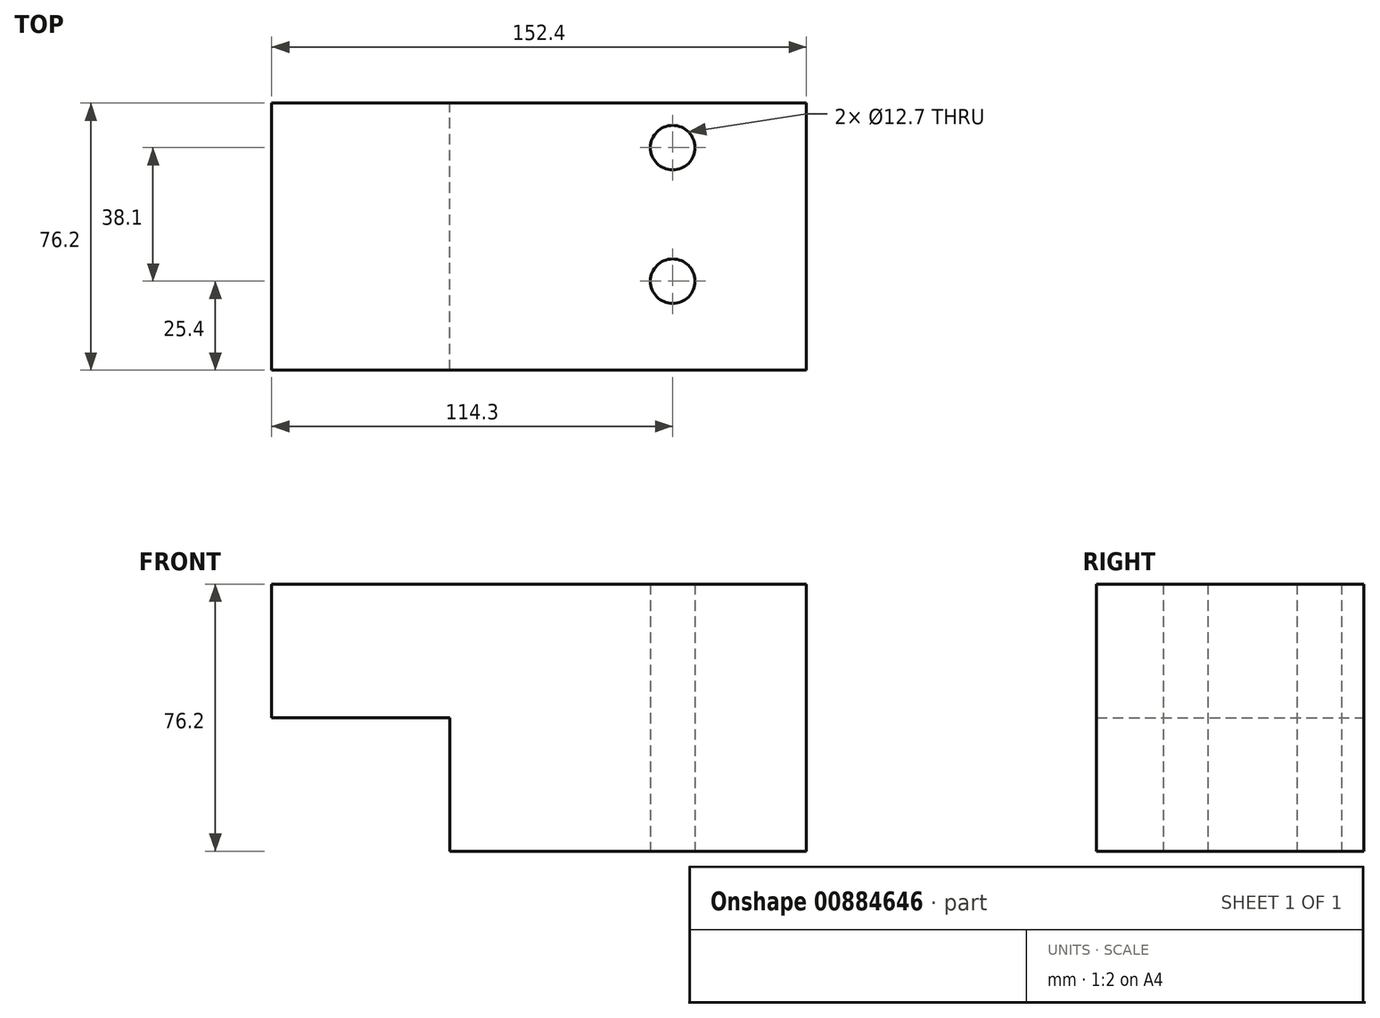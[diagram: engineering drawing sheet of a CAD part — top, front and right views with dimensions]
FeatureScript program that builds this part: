
annotation { "Feature Type Name" : "Feature", "Feature Type Description" : "" }
export const myFeature = defineFeature(function(context is Context, id is Id, definition is map)
    precondition{}
    {
        {
            var Q0;
            Q0=qCreatedBy(makeId("Top.planeOp"),FACE);
            var sketch = newSketch(context, id + "F0", { "sketchPlane" : qUnion([Q0])});
            skLineSegment(sketch, "E0.bottom", {"start": v(76.2, -38.1) * mm, "end": v(-76.2, -38.1) * mm});
            skLineSegment(sketch, "E0.top", {"start": v(76.2, 38.1) * mm, "end": v(-76.2, 38.1) * mm});
            skLineSegment(sketch, "E0.left", {"start": v(76.2, -38.1) * mm, "end": v(76.2, 38.1) * mm});
            skLineSegment(sketch, "E0.right", {"start": v(-76.2, -38.1) * mm, "end": v(-76.2, 38.1) * mm});
            skPoint(sketch, "E0.middle", {"position": v(0, 0) * mm});
            skSolve(sketch);
        }
        {
            var Q0;
            Q0 = qSketchRegion(id + "F0", true);
            extrude(context, id + "F1", {"entities" : qUnion([Q0]), "endBound" : BoundingType.SYMMETRIC, "depth" : 76.2 * mm, "offsetDistance" : 25.4 * mm});
        }
        {
            var Q0;
            Q0=makeQuery(id+"F1.opExtrude","CAP_FACE",FACE,{"disambiguationData":[OSD([sQuery(id+"F0.wireOp",EDGE,"E0.bottom"),sQuery(id+"F0.wireOp",EDGE,"E0.top"),sQuery(id+"F0.wireOp",EDGE,"E0.left"),sQuery(id+"F0.wireOp",EDGE,"E0.right")])],"isStart":true});
            var sketch = newSketch(context, id + "F2", { "sketchPlane" : qUnion([Q0])});
            skLineSegment(sketch, "E1.bottom", {"start": v(-76.2, 38.1) * mm, "end": v(-25.4, 38.1) * mm});
            skLineSegment(sketch, "E1.top", {"start": v(-76.2, -38.1) * mm, "end": v(-25.4, -38.1) * mm});
            skLineSegment(sketch, "E1.left", {"start": v(-76.2, 38.1) * mm, "end": v(-76.2, -38.1) * mm});
            skLineSegment(sketch, "E1.right", {"start": v(-25.4, 38.1) * mm, "end": v(-25.4, -38.1) * mm});
            skSolve(sketch);
        }
        {
            var Q0;
            Q0 = qSketchRegion(id + "F2", true);
            extrude(context, id + "F3", {"entities" : qUnion([Q0]), "operationType" : NewBodyOperationType.REMOVE, "oppositeDirection" : true, "depth" : 38.1 * mm, "offsetDistance" : 25.4 * mm});
        }
        {
            var Q0;
            Q0=makeQuery(id+"F1.opExtrude","CAP_FACE",FACE,{"disambiguationData":[OSD([sQuery(id+"F0.wireOp",EDGE,"E0.bottom"),sQuery(id+"F0.wireOp",EDGE,"E0.top"),sQuery(id+"F0.wireOp",EDGE,"E0.left"),sQuery(id+"F0.wireOp",EDGE,"E0.right")])],"isStart":true});
            var sketch = newSketch(context, id + "F4", { "sketchPlane" : qUnion([Q0])});
            skCircle(sketch, "E2", {"center": v(38.1, 12.7) * mm, "radius": 6.35 * mm});
            skCircle(sketch, "E3", {"center": v(38.1, -25.4) * mm, "radius": 6.35 * mm});
            skSolve(sketch);
        }
        {
            var Q0;
            Q0 = qSketchRegion(id + "F4", true);
            extrude(context, id + "F5", {"entities" : qUnion([Q0]), "operationType" : NewBodyOperationType.REMOVE, "oppositeDirection" : true, "depth" : 76.2 * mm, "offsetDistance" : 25.4 * mm});
        }
    });
